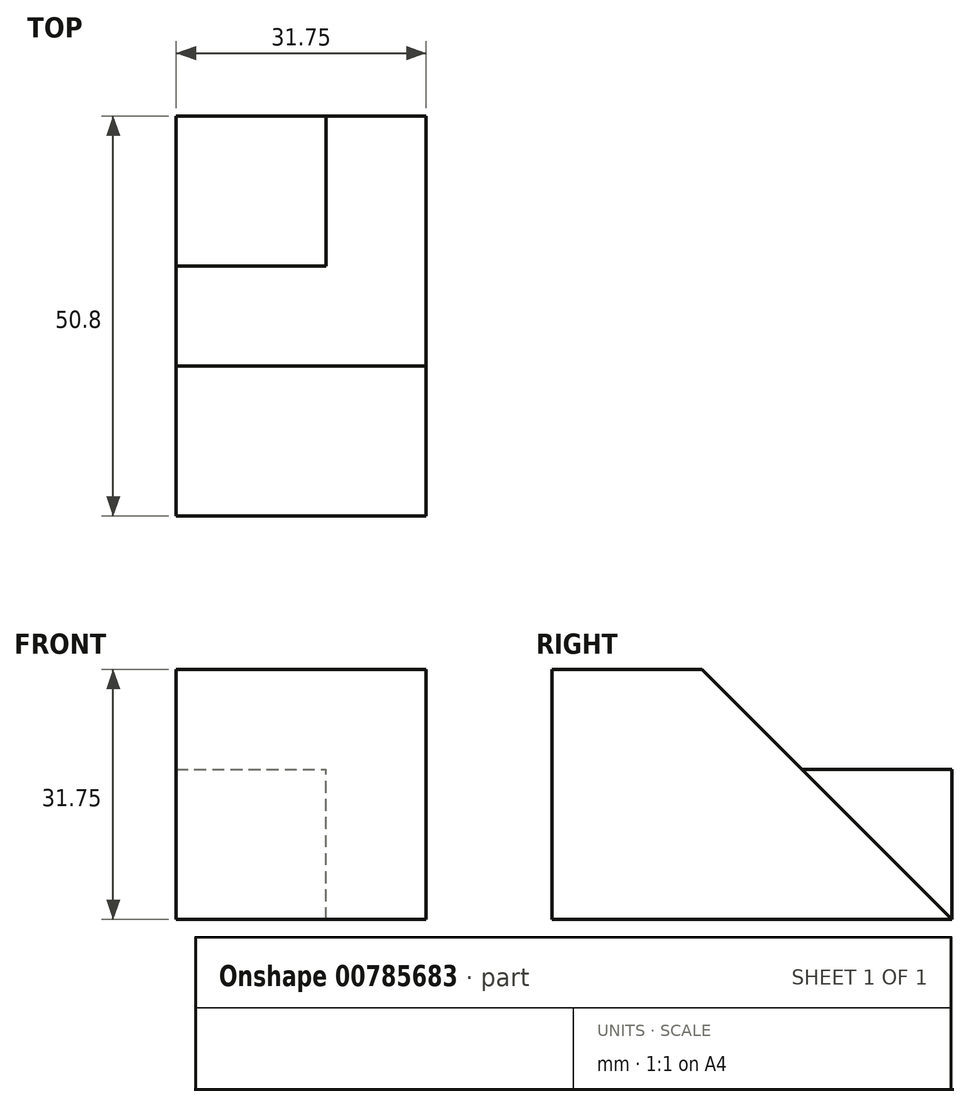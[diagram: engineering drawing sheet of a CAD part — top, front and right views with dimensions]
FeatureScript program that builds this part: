
annotation { "Feature Type Name" : "Feature", "Feature Type Description" : "" }
export const myFeature = defineFeature(function(context is Context, id is Id, definition is map)
    precondition{}
    {
        {
            var Q0;
            Q0=qCreatedBy(makeId("Front.planeOp"),FACE);
            var sketch = newSketch(context, id + "F0", { "sketchPlane" : qUnion([Q0])});
            skLineSegment(sketch, "E0", {"start": v(0, 0) * mm, "end": v(31.75, 0) * mm});
            skLineSegment(sketch, "E1", {"start": v(31.75, 0) * mm, "end": v(31.75, 31.75) * mm});
            skLineSegment(sketch, "E2", {"start": v(31.75, 31.75) * mm, "end": v(0, 31.75) * mm});
            skLineSegment(sketch, "E3", {"start": v(0, 31.75) * mm, "end": v(0, 0) * mm});
            skSolve(sketch);
        }
        {
            var Q0;
            Q0=makeQuery(id+"F0.imprint","IMPRINT",FACE,{"disambiguationData":[TD([[makeQuery(id+"F0.imprint","IMPRINT",EDGE,{"derivedFrom":sQuery(id+"F0.wireOp",EDGE,"E0")}),1.0]])]});
            extrude(context, id + "F1", {"entities" : qUnion([Q0]), "depth" : 50.8 * mm, "offsetDistance" : 25.4 * mm});
        }
        {
            var Q0;
            Q0=makeQuery(id+"F1.opExtrude","SWEPT_FACE",FACE,{"disambiguationData":[OSD([sQuery(id+"F0.wireOp",EDGE,"E1")])]});
            var sketch = newSketch(context, id + "F2", { "sketchPlane" : qUnion([Q0])});
            skLineSegment(sketch, "E4", {"start": v(-50.8, 31.75) * mm, "end": v(-31.75, 31.75) * mm});
            skLineSegment(sketch, "E5", {"start": v(-31.75, 31.75) * mm, "end": v(0, 0) * mm});
            skSolve(sketch);
        }
        {
            var Q0;
            {var subQ0=sQuery(id+"F2.wireOp",EDGE,"E5");Q0=makeQuery(id+"F2.imprint","IMPRINT",FACE,{"disambiguationData":[TD([[makeQuery(id+"F2.imprint","IMPRINT",EDGE,{"derivedFrom":subQ0}),1.0]])]});}
            extrude(context, id + "F3", {"entities" : qUnion([Q0]), "operationType" : NewBodyOperationType.REMOVE, "oppositeDirection" : true, "depth" : 12.7 * mm, "offsetDistance" : 25.4 * mm});
        }
        {
            var Q0;
            Q0=makeQuery(id+"F3.boolean.opBoolean","COPY",FACE,{"derivedFrom":makeQuery(id+"F3.opExtrude","CAP_FACE",FACE,{"disambiguationData":[OSD([sQuery(id+"F0.wireOp",EDGE,"E1"),sQuery(id+"F0.wireOp",EDGE,"E2"),sQuery(id+"F2.wireOp",EDGE,"E5")])],"isStart":false})});
            var sketch = newSketch(context, id + "F4", { "sketchPlane" : qUnion([Q0])});
            skLineSegment(sketch, "E6", {"start": v(0, 0) * mm, "end": v(0, 19.05) * mm});
            skLineSegment(sketch, "E7", {"start": v(0, 19.05) * mm, "end": v(-19.05, 19.05) * mm});
            skSolve(sketch);
        }
        {
            var Q0;
            {var subQ0=sQuery(id+"F4.wireOp",EDGE,"E7");Q0=makeQuery(id+"F4.imprint","IMPRINT",FACE,{"disambiguationData":[TD([[makeQuery(id+"F4.imprint","IMPRINT",EDGE,{"derivedFrom":subQ0}),-1.0]])]});}
            extrude(context, id + "F5", {"entities" : qUnion([Q0]), "operationType" : NewBodyOperationType.REMOVE, "oppositeDirection" : true, "depth" : 25.4 * mm, "offsetDistance" : 25.4 * mm});
        }
    });
